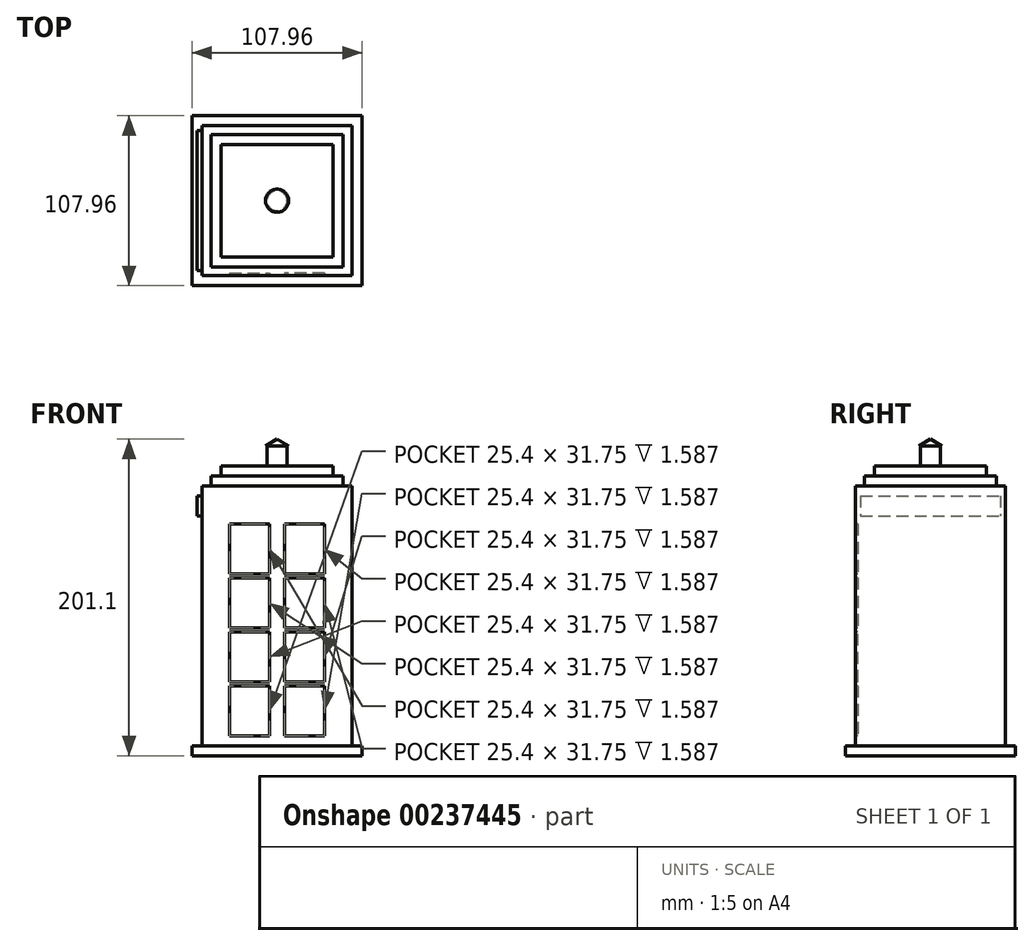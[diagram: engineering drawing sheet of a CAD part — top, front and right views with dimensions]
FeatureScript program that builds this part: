
annotation { "Feature Type Name" : "Feature", "Feature Type Description" : "" }
export const myFeature = defineFeature(function(context is Context, id is Id, definition is map)
    precondition{}
    {
        {
            var Q0;
            Q0=qCreatedBy(makeId("Top.planeOp"),FACE);
            var sketch = newSketch(context, id + "F0", { "sketchPlane" : qUnion([Q0])});
            skLineSegment(sketch, "E0.bottom", {"start": v(-53.97, 53.98) * mm, "end": v(53.98, 53.98) * mm});
            skLineSegment(sketch, "E0.top", {"start": v(-53.98, -53.98) * mm, "end": v(53.97, -53.98) * mm});
            skLineSegment(sketch, "E0.left", {"start": v(-53.97, 53.98) * mm, "end": v(-53.98, -53.98) * mm});
            skLineSegment(sketch, "E0.right", {"start": v(53.98, 53.98) * mm, "end": v(53.97, -53.98) * mm});
            skPoint(sketch, "E0.middle", {"position": v(0, 0) * mm});
            skSolve(sketch);
        }
        {
            var Q0;
            Q0 = qSketchRegion(id + "F0", true);
            extrude(context, id + "F1", {"entities" : qUnion([Q0]), "depth" : 6.35 * mm});
        }
        {
            var Q0;
            Q0=makeQuery(id+"F1.opExtrude","CAP_FACE",FACE,{"disambiguationData":[OSD([sQuery(id+"F0.wireOp",EDGE,"E0.bottom"),sQuery(id+"F0.wireOp",EDGE,"E0.top"),sQuery(id+"F0.wireOp",EDGE,"E0.left"),sQuery(id+"F0.wireOp",EDGE,"E0.right")])],"isStart":false});
            var sketch = newSketch(context, id + "F2", { "sketchPlane" : qUnion([Q0])});
            skLineSegment(sketch, "E1.0", {"start": v(-47.62, 47.62) * mm, "end": v(-47.63, -47.62) * mm});
            skLineSegment(sketch, "E1.1", {"start": v(47.63, 47.62) * mm, "end": v(-47.62, 47.62) * mm});
            skLineSegment(sketch, "E1.2", {"start": v(47.62, -47.62) * mm, "end": v(47.63, 47.62) * mm});
            skLineSegment(sketch, "E1.3", {"start": v(-47.63, -47.62) * mm, "end": v(47.62, -47.62) * mm});
            skSolve(sketch);
        }
        {
            var Q0;
            Q0 = qSketchRegion(id + "F2", true);
            extrude(context, id + "F3", {"entities" : qUnion([Q0]), "operationType" : NewBodyOperationType.ADD, "depth" : 165.1 * mm});
        }
        {
            var Q0;
            Q0=makeQuery(id+"F3.opExtrude","CAP_FACE",FACE,{"disambiguationData":[OSD([sQuery(id+"F2.wireOp",EDGE,"E1.0"),sQuery(id+"F2.wireOp",EDGE,"E1.1"),sQuery(id+"F2.wireOp",EDGE,"E1.2"),sQuery(id+"F2.wireOp",EDGE,"E1.3")])],"isStart":false});
            var sketch = newSketch(context, id + "F4", { "sketchPlane" : qUnion([Q0])});
            skLineSegment(sketch, "E2.0", {"start": v(-42.04, 42.04) * mm, "end": v(-42.04, -42.04) * mm});
            skLineSegment(sketch, "E2.1", {"start": v(42.04, 42.04) * mm, "end": v(-42.04, 42.04) * mm});
            skLineSegment(sketch, "E2.2", {"start": v(42.04, -42.04) * mm, "end": v(42.04, 42.04) * mm});
            skLineSegment(sketch, "E2.3", {"start": v(-42.04, -42.04) * mm, "end": v(42.04, -42.04) * mm});
            skSolve(sketch);
        }
        {
            var Q0;
            Q0 = qSketchRegion(id + "F4", true);
            extrude(context, id + "F5", {"entities" : qUnion([Q0]), "operationType" : NewBodyOperationType.ADD, "depth" : 6.35 * mm});
        }
        {
            var Q0;
            Q0=makeQuery(id+"F5.opExtrude","CAP_FACE",FACE,{"disambiguationData":[OSD([sQuery(id+"F4.wireOp",EDGE,"E2.0"),sQuery(id+"F4.wireOp",EDGE,"E2.1"),sQuery(id+"F4.wireOp",EDGE,"E2.2"),sQuery(id+"F4.wireOp",EDGE,"E2.3")])],"isStart":false});
            var sketch = newSketch(context, id + "F6", { "sketchPlane" : qUnion([Q0])});
            skLineSegment(sketch, "E3.0", {"start": v(-35.69, 35.69) * mm, "end": v(-35.69, -35.69) * mm});
            skLineSegment(sketch, "E3.1", {"start": v(35.69, 35.69) * mm, "end": v(-35.69, 35.69) * mm});
            skLineSegment(sketch, "E3.2", {"start": v(35.69, -35.69) * mm, "end": v(35.69, 35.69) * mm});
            skLineSegment(sketch, "E3.3", {"start": v(-35.69, -35.69) * mm, "end": v(35.69, -35.69) * mm});
            skSolve(sketch);
        }
        {
            var Q0;
            Q0 = qSketchRegion(id + "F6", true);
            extrude(context, id + "F7", {"entities" : qUnion([Q0]), "operationType" : NewBodyOperationType.ADD, "depth" : 6.35 * mm});
        }
        {
            var Q0;
            Q0=makeQuery(id+"F3.opExtrude","SWEPT_FACE",FACE,{"disambiguationData":[OSD([sQuery(id+"F2.wireOp",EDGE,"E1.0")])]});
            var sketch = newSketch(context, id + "F8", { "sketchPlane" : qUnion([Q0])});
            skLineSegment(sketch, "E4.bottom", {"start": v(44.45, 165.12) * mm, "end": v(-44.45, 165.12) * mm});
            skLineSegment(sketch, "E4.top", {"start": v(44.45, 152.42) * mm, "end": v(-44.45, 152.42) * mm});
            skLineSegment(sketch, "E4.left", {"start": v(44.45, 165.12) * mm, "end": v(44.45, 152.42) * mm});
            skLineSegment(sketch, "E4.right", {"start": v(-44.45, 165.12) * mm, "end": v(-44.45, 152.42) * mm});
            skPoint(sketch, "E4.middle", {"position": v(0, 158.77) * mm});
            skPoint(sketch, "E4.middle.positionSnap0", {"position": v(0, 171.45) * mm});
            skPoint(sketch, "E4.centerSnap0", {"position": v(0, 171.45) * mm});
            skSolve(sketch);
        }
        {
            var Q0;
            Q0 = qSketchRegion(id + "F8", true);
            extrude(context, id + "F9", {"entities" : qUnion([Q0]), "operationType" : NewBodyOperationType.ADD, "depth" : 3.17 * mm});
        }
        {
            var Q0;
            Q0=qCreatedBy(makeId("Front.planeOp"),FACE);
            var sketch = newSketch(context, id + "F10", { "sketchPlane" : qUnion([Q0])});
            skLineSegment(sketch, "E5", {"start": v(0, 0) * mm, "end": v(0, 169.81) * mm});
            skSolve(sketch);
        }
        {
            var Q0;
            Q0=makeQuery(id+"F7.opExtrude","CAP_FACE",FACE,{"disambiguationData":[OSD([sQuery(id+"F6.wireOp",EDGE,"E3.0"),sQuery(id+"F6.wireOp",EDGE,"E3.1"),sQuery(id+"F6.wireOp",EDGE,"E3.2"),sQuery(id+"F6.wireOp",EDGE,"E3.3")])],"isStart":false});
            var sketch = newSketch(context, id + "F11", { "sketchPlane" : qUnion([Q0])});
            skCircle(sketch, "E6", {"center": v(0, 0) * mm, "radius": 6.35 * mm});
            skSolve(sketch);
        }
        {
            var Q0;
            Q0 = qSketchRegion(id + "F11", true);
            extrude(context, id + "F12", {"entities" : qUnion([Q0]), "operationType" : NewBodyOperationType.ADD, "depth" : 12.7 * mm});
        }
        {
            var Q0;
            Q0=makeQuery(id+"F12.opExtrude","CAP_FACE",FACE,{"disambiguationData":[OSD([sQuery(id+"F11.wireOp",EDGE,"E6")])],"isStart":false});
            var sketch = newSketch(context, id + "F13", { "sketchPlane" : qUnion([Q0])});
            skCircle(sketch, "E7.0", {"center": v(0, 0) * mm, "radius": 7.37 * mm});
            skSolve(sketch);
        }
        {
            var Q0;
            Q0 = qSketchRegion(id + "F13", true);
            extrude(context, id + "F14", {"entities" : qUnion([Q0]), "operationType" : NewBodyOperationType.ADD, "depth" : 25.4 * mm, "hasDraft" : true, "draftAngle" : 60 * degree, "draftPullDirection" : true});
        }
        {
            var Q0;
            Q0=makeQuery(id+"F3.opExtrude","SWEPT_FACE",FACE,{"disambiguationData":[OSD([sQuery(id+"F2.wireOp",EDGE,"E1.3")])]});
            var sketch = newSketch(context, id + "F15", { "sketchPlane" : qUnion([Q0])});
            skLineSegment(sketch, "E8.bottom", {"start": v(-30.16, 44.45) * mm, "end": v(-4.76, 44.45) * mm});
            skLineSegment(sketch, "E8.top", {"start": v(-30.16, 12.7) * mm, "end": v(-4.76, 12.7) * mm});
            skLineSegment(sketch, "E8.left", {"start": v(-30.16, 44.45) * mm, "end": v(-30.16, 12.7) * mm});
            skLineSegment(sketch, "E8.right", {"start": v(-4.76, 44.45) * mm, "end": v(-4.76, 12.7) * mm});
            skPoint(sketch, "E8.middle", {"position": v(-17.46, 28.58) * mm});
            skLineSegment(sketch, "E9.0.1.0", {"start": v(-30.16, 78.74) * mm, "end": v(-4.76, 78.74) * mm});
            skLineSegment(sketch, "E9.0.1.1", {"start": v(-4.76, 78.74) * mm, "end": v(-4.76, 47) * mm});
            skLineSegment(sketch, "E9.0.1.2", {"start": v(-30.16, 47) * mm, "end": v(-4.76, 47) * mm});
            skLineSegment(sketch, "E9.0.1.3", {"start": v(-30.16, 78.74) * mm, "end": v(-30.16, 47) * mm});
            skLineSegment(sketch, "E9.0.2.0", {"start": v(-30.16, 113.03) * mm, "end": v(-4.76, 113.03) * mm});
            skLineSegment(sketch, "E9.0.2.1", {"start": v(-4.76, 113.03) * mm, "end": v(-4.76, 81.28) * mm});
            skLineSegment(sketch, "E9.0.2.2", {"start": v(-30.16, 81.28) * mm, "end": v(-4.76, 81.28) * mm});
            skLineSegment(sketch, "E9.0.2.3", {"start": v(-30.16, 113.03) * mm, "end": v(-30.16, 81.28) * mm});
            skLineSegment(sketch, "E9.direction2", {"start": v(-30.16, 44.45) * mm, "end": v(-30.16, 78.74) * mm, "construction": true});
            skLineSegment(sketch, "E10.0.0.3", {"start": v(-30.16, 147.32) * mm, "end": v(-4.76, 147.32) * mm});
            skLineSegment(sketch, "E10.3.0.3", {"start": v(-4.76, 147.32) * mm, "end": v(-4.76, 115.57) * mm});
            skLineSegment(sketch, "E10.6.0.3", {"start": v(-30.16, 115.57) * mm, "end": v(-4.76, 115.57) * mm});
            skLineSegment(sketch, "E10.9.0.3", {"start": v(-30.16, 147.32) * mm, "end": v(-30.16, 115.57) * mm});
            skLineSegment(sketch, "E11.MirrorCS", {"start": v(4.76, 113.03) * mm, "end": v(4.76, 81.28) * mm});
            skLineSegment(sketch, "E12.MirrorCS", {"start": v(4.76, 147.32) * mm, "end": v(4.76, 115.57) * mm});
            skLineSegment(sketch, "E13.MirrorCS", {"start": v(30.16, 147.32) * mm, "end": v(4.76, 147.32) * mm});
            skLineSegment(sketch, "E14.MirrorCS", {"start": v(30.16, 147.32) * mm, "end": v(30.16, 115.57) * mm});
            skLineSegment(sketch, "E15.MirrorCS", {"start": v(30.16, 115.57) * mm, "end": v(4.76, 115.57) * mm});
            skLineSegment(sketch, "E16.MirrorCS", {"start": v(30.16, 113.03) * mm, "end": v(4.76, 113.03) * mm});
            skLineSegment(sketch, "E17.MirrorCS", {"start": v(30.16, 113.03) * mm, "end": v(30.16, 81.28) * mm});
            skLineSegment(sketch, "E18.MirrorCS", {"start": v(30.16, 81.28) * mm, "end": v(4.76, 81.28) * mm});
            skLineSegment(sketch, "E19.MirrorCS", {"start": v(30.16, 78.74) * mm, "end": v(4.76, 78.74) * mm});
            skLineSegment(sketch, "E20.MirrorCS", {"start": v(30.16, 44.45) * mm, "end": v(30.16, 78.74) * mm});
            skLineSegment(sketch, "E21.MirrorCS", {"start": v(4.76, 78.74) * mm, "end": v(4.76, 47) * mm});
            skLineSegment(sketch, "E22.MirrorCS", {"start": v(30.16, 47) * mm, "end": v(4.76, 47) * mm});
            skLineSegment(sketch, "E23.MirrorCS", {"start": v(30.16, 44.45) * mm, "end": v(4.76, 44.45) * mm});
            skLineSegment(sketch, "E24.MirrorCS", {"start": v(30.16, 44.45) * mm, "end": v(30.16, 12.7) * mm});
            skLineSegment(sketch, "E25.MirrorCS", {"start": v(30.16, 12.7) * mm, "end": v(4.76, 12.7) * mm});
            skLineSegment(sketch, "E26.MirrorCS", {"start": v(4.76, 44.45) * mm, "end": v(4.76, 12.7) * mm});
            skSolve(sketch);
        }
        {
            var Q0;
            Q0 = qSketchRegion(id + "F15", true);
            extrude(context, id + "F16", {"entities" : qUnion([Q0]), "operationType" : NewBodyOperationType.REMOVE, "oppositeDirection" : true, "depth" : 1.59 * mm});
        }
    });
